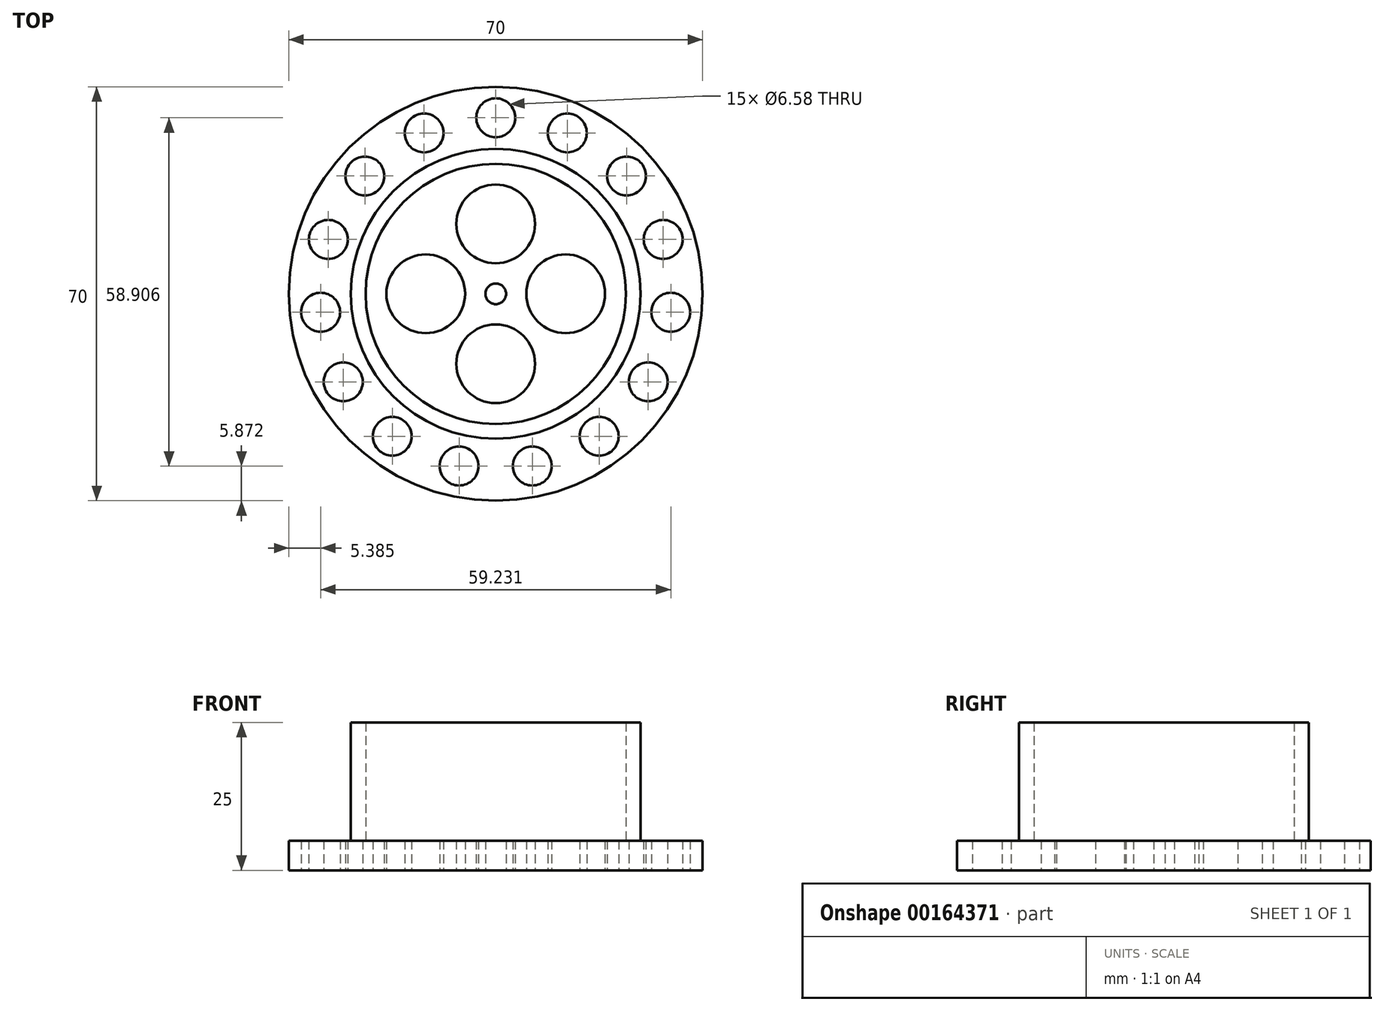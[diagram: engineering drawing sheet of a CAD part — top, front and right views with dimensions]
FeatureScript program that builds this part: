
annotation { "Feature Type Name" : "Feature", "Feature Type Description" : "" }
export const myFeature = defineFeature(function(context is Context, id is Id, definition is map)
    precondition{}
    {
        {
            var Q0;
            Q0=qCreatedBy(makeId("Top.planeOp"),FACE);
            var sketch = newSketch(context, id + "F0", { "sketchPlane" : qUnion([Q0])});
            skCircle(sketch, "E0", {"center": v(0, 0) * mm, "radius": 35 * mm});
            skCircle(sketch, "E1", {"center": v(0, 0) * mm, "radius": 22 * mm});
            skCircle(sketch, "E2", {"center": v(0, 0) * mm, "radius": 24.5 * mm});
            skCircle(sketch, "E3", {"center": v(0, 0) * mm, "radius": 1.75 * mm});
            skCircle(sketch, "E4", {"center": v(0, 11.83) * mm, "radius": 6.66 * mm});
            skCircle(sketch, "E5", {"center": v(0, 29.78) * mm, "radius": 3.29 * mm});
            skCircle(sketch, "E6.1.0", {"center": v(-12.11, 27.2) * mm, "radius": 3.29 * mm});
            skCircle(sketch, "E6.2.0", {"center": v(-22.13, 19.93) * mm, "radius": 3.29 * mm});
            skCircle(sketch, "E6.3.0", {"center": v(-28.32, 9.2) * mm, "radius": 3.29 * mm});
            skCircle(sketch, "E6.4.0", {"center": v(-29.62, -3.11) * mm, "radius": 3.29 * mm});
            skCircle(sketch, "E6.5.0", {"center": v(-25.79, -14.89) * mm, "radius": 3.29 * mm});
            skCircle(sketch, "E6.6.0", {"center": v(-17.5, -24.1) * mm, "radius": 3.29 * mm});
            skCircle(sketch, "E6.7.0", {"center": v(-6.2, -29.13) * mm, "radius": 3.29 * mm});
            skCircle(sketch, "E6.8.0", {"center": v(6.2, -29.13) * mm, "radius": 3.29 * mm});
            skCircle(sketch, "E6.9.0", {"center": v(17.5, -24.1) * mm, "radius": 3.29 * mm});
            skCircle(sketch, "E6.10.0", {"center": v(25.79, -14.89) * mm, "radius": 3.29 * mm});
            skCircle(sketch, "E6.11.0", {"center": v(29.62, -3.11) * mm, "radius": 3.29 * mm});
            skCircle(sketch, "E6.12.0", {"center": v(28.32, 9.2) * mm, "radius": 3.29 * mm});
            skCircle(sketch, "E6.13.0", {"center": v(22.13, 19.93) * mm, "radius": 3.29 * mm});
            skCircle(sketch, "E6.14.0", {"center": v(12.11, 27.2) * mm, "radius": 3.29 * mm});
            skCircle(sketch, "E7.1.0", {"center": v(-11.83, 0) * mm, "radius": 6.66 * mm});
            skCircle(sketch, "E7.2.0", {"center": v(0, -11.83) * mm, "radius": 6.66 * mm});
            skCircle(sketch, "E7.3.0", {"center": v(11.83, 0) * mm, "radius": 6.66 * mm});
            skSolve(sketch);
        }
        {
            var Q0;
            Q0=qSketchRegion(id+"F0",true);
            var Q1;
            Q1=makeQuery(id+"F0.imprint","IMPRINT",FACE,{"disambiguationData":[TD([[makeQuery(id+"F0.imprint","IMPRINT",EDGE,{"derivedFrom":sQuery(id+"F0.wireOp",EDGE,"E1")}),1.0]])]});
            var Q2;
            Q2=makeQuery(id+"F0.imprint","IMPRINT",FACE,{"disambiguationData":[TD([[makeQuery(id+"F0.imprint","IMPRINT",EDGE,{"derivedFrom":sQuery(id+"F0.wireOp",EDGE,"E1")}),-1.0]])]});
            extrude(context, id + "F1", {"entities" : qUnion([Q0, Q1, Q2]), "depth" : 5 * mm});
        }
        {
            var Q0;
            Q0=makeQuery(id+"F0.imprint","IMPRINT",FACE,{"disambiguationData":[TD([[makeQuery(id+"F0.imprint","IMPRINT",EDGE,{"derivedFrom":sQuery(id+"F0.wireOp",EDGE,"E1")}),-1.0]])]});
            extrude(context, id + "F2", {"entities" : qUnion([Q0]), "operationType" : NewBodyOperationType.ADD, "depth" : 25 * mm, "offsetDistance" : 25 * mm});
        }
        {
            var Q0;
            Q0=makeQuery(id+"F0.imprint","IMPRINT",FACE,{"disambiguationData":[TD([[makeQuery(id+"F0.imprint","IMPRINT",EDGE,{"derivedFrom":sQuery(id+"F0.wireOp",EDGE,"E0")}),1.0]])]});
            extrude(context, id + "F3", {"entities" : qUnion([Q0]), "operationType" : NewBodyOperationType.ADD, "depth" : 3 * mm});
        }
    });
